# Revit family: 238
name_source: partatom
category: Lighting Fixtures
revit_build: Autodesk Revit 2014 (Build: 20130308_1515(x64)
units: mm (PartAtom-declared; Revit-internal decimal feet)

## types (1)
- 238
    Apparent Load = 70 VA
    Assembly Code = D5020200
    Color Filter = 16777215
    Connector Description = Lighting Connector
    Default Elevation = 1219.2 mm  [stored 4 ft]
    Description = The innovative new 238 LED is an efficient low energy wellglass designed for general purpose low and medium bay illumination. With an instant on output and 80,000 maintenance free hours (L70), it offers significant benefits over the conventional product. The luminaire has a side mounted increased safety terminal chamber eliminating the need for flameproof glands. The wide ambient temperature range makes the 238 LED suitable for extreme environmental conditions.
    Dimming Lamp Color Temperature Shift = <None>
    Emit Shape Visible in Rendering = No
    Emit from Circle Diameter = 50 mm  [stored 0.164042 ft]
    Features = Installation to gas groups IIA and IIB.
Highly Energy Efficient.
Instant on - crisp white light output.
80,000 maintenance free hours.
Low temperature applications to -40°C.
Ex e terminal chamber.
    Fixture distribution = Direct
    Glass = Hubbell - Glass
    Height = 535 mm
    Housing Material = Paint - Hubbell - White Texture
    IP Rating = IP66/67
    Inner Length = 200 mm  [stored 0.656168 ft]
    LED = Paint - Hubbell - Yellow
    Lamp = LED
    Length = 380 mm  [stored 1.24672 ft]
    Load Classification = Lighting
    Manufacturer = Chalmit
    Model = 238
    Mounting = Paint - Hubbell - Light Silver
    Photometric Web File = CHL_238D_09L_LE.ies
    Power Factor = 1
    Product Documentation Link = https://hubbellcdn.com
    Product Link = https://www.hubbell.com
    Reflector Finish = Hubbell - White Glass
    Tilt Angle = 90.00°
    URL = https://www.hubbell.com
    Voltage = 120 V
    Warranty = 5 years Warranty
    Wattage Comments = 70W
    Watts = 70 W
    Width = 280 mm  [stored 0.918635 ft]

note: [stored X ft] marks values corroborated as IEEE doubles in the binary element streams (Revit-internal decimal feet)

## geometry (parser evidence)
native form markers: Sweep x2
no freeform markers — native parametric forms only
